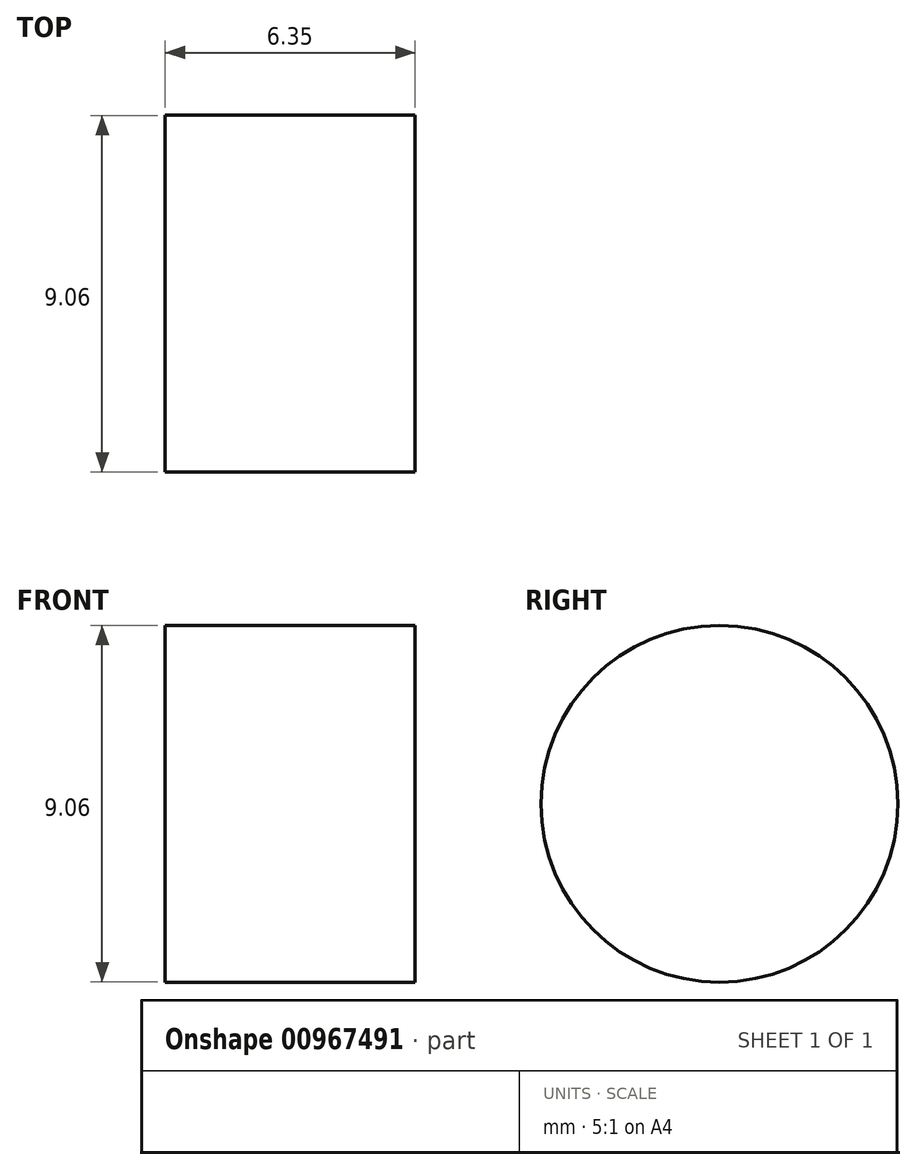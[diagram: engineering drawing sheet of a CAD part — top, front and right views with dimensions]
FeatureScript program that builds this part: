
annotation { "Feature Type Name" : "Feature", "Feature Type Description" : "" }
export const myFeature = defineFeature(function(context is Context, id is Id, definition is map)
    precondition{}
    {
        {
            var Q0;
            Q0=qCreatedBy(makeId("Front.planeOp"),FACE);
            var sketch = newSketch(context, id + "F0", { "sketchPlane" : qUnion([Q0])});
            skLineSegment(sketch, "E0", {"start": v(0, 0) * mm, "end": v(0, 127) * mm});
            skLineSegment(sketch, "E1", {"start": v(0, 127) * mm, "end": v(-6.35, 127) * mm});
            skLineSegment(sketch, "E2", {"start": v(-6.35, 127) * mm, "end": v(-6.35, 0) * mm});
            skLineSegment(sketch, "E3", {"start": v(-149.06, 0) * mm, "end": v(151.45, 0) * mm, "construction": true});
            skLineSegment(sketch, "E4.MirrorCS", {"start": v(-6.35, -127) * mm, "end": v(-6.35, 0) * mm});
            skLineSegment(sketch, "E5.MirrorCS", {"start": v(0, 0) * mm, "end": v(0, -127) * mm});
            skLineSegment(sketch, "E6.MirrorCS", {"start": v(0, -127) * mm, "end": v(-6.35, -127) * mm});
            skSolve(sketch);
        }
        {
            var Q0;
            Q0=makeQuery(id+"F0.imprint","IMPRINT",FACE,{"disambiguationData":[TD([[makeQuery(id+"F0.imprint","IMPRINT",EDGE,{"derivedFrom":sQuery(id+"F0.wireOp",EDGE,"E0")}),1.0]])]});
            extrude(context, id + "F1", {"entities" : qUnion([Q0]), "endBound" : BoundingType.SYMMETRIC, "depth" : 152.4 * mm, "offsetDistance" : 25.4 * mm});
        }
        {
            var Q0;
            Q0=makeQuery(id+"F1.opExtrude","SWEPT_FACE",FACE,{"disambiguationData":[OSD([sQuery(id+"F0.wireOp",EDGE,"E0"),sQuery(id+"F0.wireOp",EDGE,"E5.MirrorCS")])]});
            var sketch = newSketch(context, id + "F2", { "sketchPlane" : qUnion([Q0])});
            skCircle(sketch, "E7", {"center": v(0, -85.42) * mm, "radius": 4.53 * mm});
            skLineSegment(sketch, "E8", {"start": v(0, -85.42) * mm, "end": v(41.2, -85.42) * mm, "construction": true});
            skLineSegment(sketch, "E9", {"start": v(-175.24, 0) * mm, "end": v(180.75, 0) * mm, "construction": true});
            skCircle(sketch, "E10.MirrorC", {"center": v(0, 85.42) * mm, "radius": 4.53 * mm});
            skSolve(sketch);
        }
        {
            var Q0;
            Q0=makeQuery(id+"F2.imprint","IMPRINT",FACE,{"disambiguationData":[TD([[makeQuery(id+"F2.imprint","IMPRINT",EDGE,{"derivedFrom":sQuery(id+"F2.wireOp",EDGE,"oYp43fNF-x1mv-ykNY-2NdD-OxMKOIU3K59v")}),1.0]])]});
            var Q1;
            Q1=makeQuery(id+"F2.imprint","IMPRINT",FACE,{"disambiguationData":[TD([[makeQuery(id+"F2.imprint","IMPRINT",EDGE,{"derivedFrom":sQuery(id+"F2.wireOp",EDGE,"E7")}),1.0]])]});
            var Q2;
            Q2=makeQuery(id+"F2.imprint","IMPRINT",FACE,{"disambiguationData":[TD([[makeQuery(id+"F2.imprint","IMPRINT",EDGE,{"derivedFrom":sQuery(id+"F2.wireOp",EDGE,"3c9c32e5-bcbf-44e3-ad1f-b25b58e2b3da0.MirrorC")}),-1.0]])]});
            var Q3;
            Q3=makeQuery(id+"F2.imprint","IMPRINT",FACE,{"disambiguationData":[TD([[makeQuery(id+"F2.imprint","IMPRINT",EDGE,{"derivedFrom":sQuery(id+"F2.wireOp",EDGE,"dc575471-8594-4d59-aef2-c47dee9ce68c0.MirrorC")}),-1.0]])]});
            var Q4;
            Q4=makeQuery(id+"F2.imprint","IMPRINT",FACE,{"disambiguationData":[TD([[makeQuery(id+"F2.imprint","IMPRINT",EDGE,{"derivedFrom":sQuery(id+"F2.wireOp",EDGE,"E10.MirrorC")}),-1.0]])]});
            var Q5;
            Q5=makeQuery(id+"F2.imprint","IMPRINT",FACE,{"disambiguationData":[TD([[makeQuery(id+"F2.imprint","IMPRINT",EDGE,{"derivedFrom":sQuery(id+"F2.wireOp",EDGE,"68586926-7c13-4228-a31a-19db4b6c24a10.MirrorC")}),1.0]])]});
            extrude(context, id + "F3", {"entities" : qUnion([Q0, Q1, Q2, Q3, Q4, Q5]), "operationType" : NewBodyOperationType.REMOVE, "endBound" : BoundingType.THROUGH_ALL, "oppositeDirection" : true, "depth" : 25.4 * mm, "offsetDistance" : 25.4 * mm});
        }
    });
